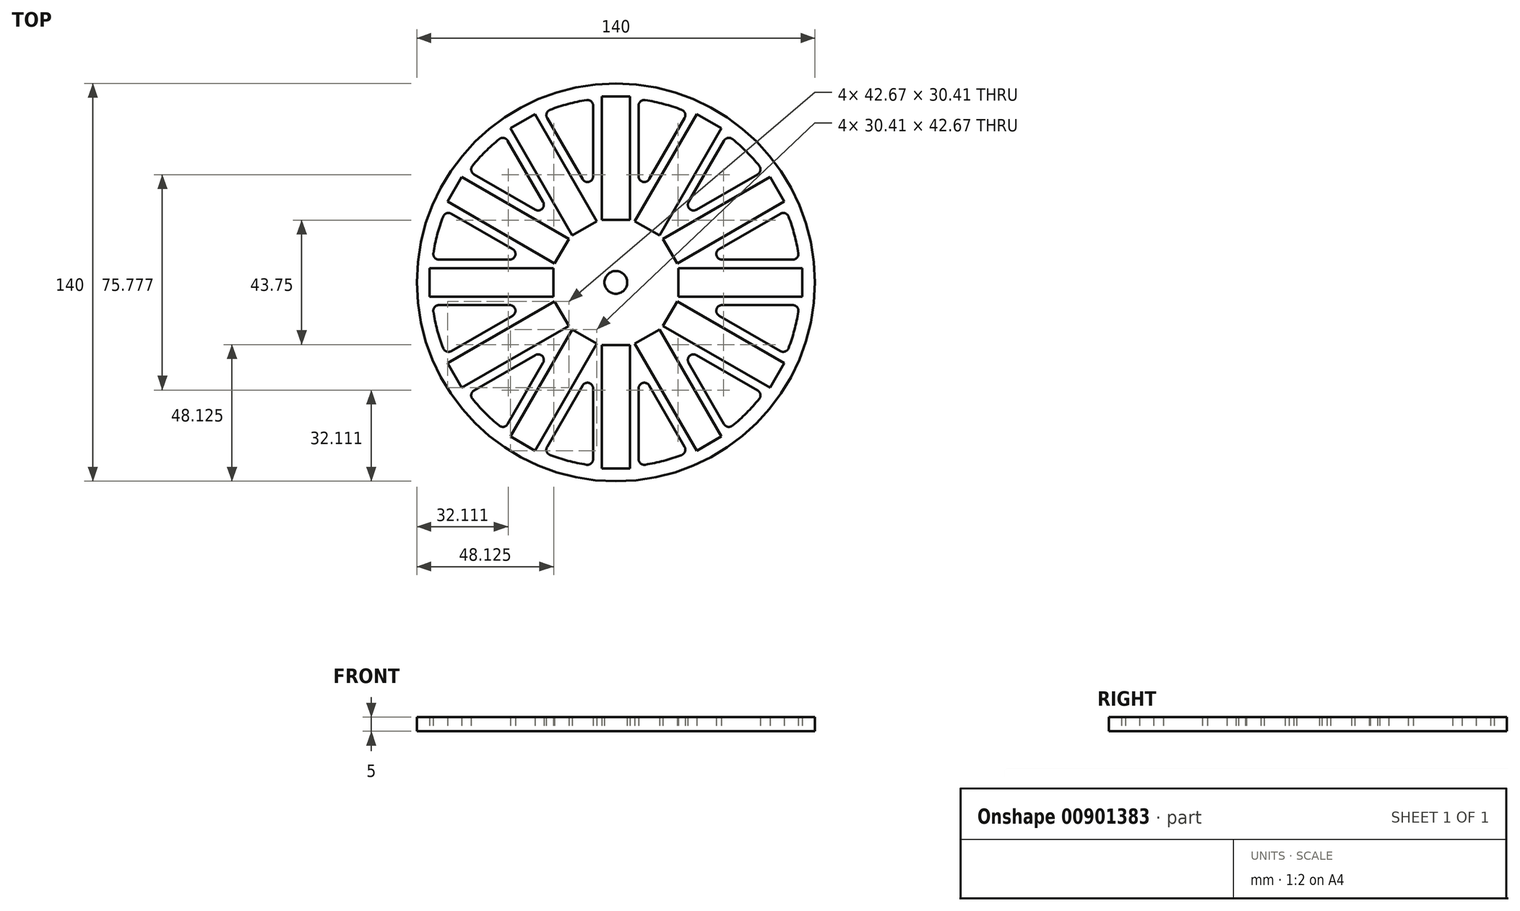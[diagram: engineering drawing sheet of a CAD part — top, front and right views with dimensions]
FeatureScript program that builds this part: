
annotation { "Feature Type Name" : "Feature", "Feature Type Description" : "" }
export const myFeature = defineFeature(function(context is Context, id is Id, definition is map)
    precondition{}
    {
        {
            var Q0;
            Q0=qCreatedBy(makeId("Top.planeOp"),FACE);
            var sketch = newSketch(context, id + "F0", { "sketchPlane" : qUnion([Q0])});
            skLineSegment(sketch, "E0.bottom", {"start": v(65.5, 5) * mm, "end": v(22, 5) * mm});
            skLineSegment(sketch, "E0.top", {"start": v(65.5, -5) * mm, "end": v(22, -5) * mm});
            skLineSegment(sketch, "E0.left", {"start": v(65.5, 5) * mm, "end": v(65.5, -5) * mm});
            skLineSegment(sketch, "E0.right", {"start": v(22, 5) * mm, "end": v(22, -5) * mm});
            skCircle(sketch, "E1", {"center": v(0, 0) * mm, "radius": 4 * mm});
            skLineSegment(sketch, "E2.1.0", {"start": v(54.22, 37.08) * mm, "end": v(59.22, 28.42) * mm});
            skLineSegment(sketch, "E2.1.1", {"start": v(54.22, 37.08) * mm, "end": v(16.55, 15.33) * mm});
            skLineSegment(sketch, "E2.1.2", {"start": v(59.22, 28.42) * mm, "end": v(21.55, 6.67) * mm});
            skLineSegment(sketch, "E2.1.3", {"start": v(16.55, 15.33) * mm, "end": v(21.55, 6.67) * mm});
            skLineSegment(sketch, "E2.2.0", {"start": v(28.42, 59.22) * mm, "end": v(37.08, 54.22) * mm});
            skLineSegment(sketch, "E2.2.1", {"start": v(28.42, 59.22) * mm, "end": v(6.67, 21.55) * mm});
            skLineSegment(sketch, "E2.2.2", {"start": v(37.08, 54.22) * mm, "end": v(15.33, 16.55) * mm});
            skLineSegment(sketch, "E2.2.3", {"start": v(6.67, 21.55) * mm, "end": v(15.33, 16.55) * mm});
            skLineSegment(sketch, "E2.3.0", {"start": v(-5, 65.5) * mm, "end": v(5, 65.5) * mm});
            skLineSegment(sketch, "E2.3.1", {"start": v(-5, 65.5) * mm, "end": v(-5, 22) * mm});
            skLineSegment(sketch, "E2.3.2", {"start": v(5, 65.5) * mm, "end": v(5, 22) * mm});
            skLineSegment(sketch, "E2.3.3", {"start": v(-5, 22) * mm, "end": v(5, 22) * mm});
            skLineSegment(sketch, "E2.4.0", {"start": v(-37.08, 54.22) * mm, "end": v(-28.42, 59.22) * mm});
            skLineSegment(sketch, "E2.4.1", {"start": v(-37.08, 54.22) * mm, "end": v(-15.33, 16.55) * mm});
            skLineSegment(sketch, "E2.4.2", {"start": v(-28.42, 59.22) * mm, "end": v(-6.67, 21.55) * mm});
            skLineSegment(sketch, "E2.4.3", {"start": v(-15.33, 16.55) * mm, "end": v(-6.67, 21.55) * mm});
            skLineSegment(sketch, "E2.5.0", {"start": v(-59.22, 28.42) * mm, "end": v(-54.22, 37.08) * mm});
            skLineSegment(sketch, "E2.5.1", {"start": v(-59.22, 28.42) * mm, "end": v(-21.55, 6.67) * mm});
            skLineSegment(sketch, "E2.5.2", {"start": v(-54.22, 37.08) * mm, "end": v(-16.55, 15.33) * mm});
            skLineSegment(sketch, "E2.5.3", {"start": v(-21.55, 6.67) * mm, "end": v(-16.55, 15.33) * mm});
            skLineSegment(sketch, "E2.6.0", {"start": v(-65.5, -5) * mm, "end": v(-65.5, 5) * mm});
            skLineSegment(sketch, "E2.6.1", {"start": v(-65.5, -5) * mm, "end": v(-22, -5) * mm});
            skLineSegment(sketch, "E2.6.2", {"start": v(-65.5, 5) * mm, "end": v(-22, 5) * mm});
            skLineSegment(sketch, "E2.6.3", {"start": v(-22, -5) * mm, "end": v(-22, 5) * mm});
            skLineSegment(sketch, "E2.7.0", {"start": v(-54.22, -37.08) * mm, "end": v(-59.22, -28.42) * mm});
            skLineSegment(sketch, "E2.7.1", {"start": v(-54.22, -37.08) * mm, "end": v(-16.55, -15.33) * mm});
            skLineSegment(sketch, "E2.7.2", {"start": v(-59.22, -28.42) * mm, "end": v(-21.55, -6.67) * mm});
            skLineSegment(sketch, "E2.7.3", {"start": v(-16.55, -15.33) * mm, "end": v(-21.55, -6.67) * mm});
            skLineSegment(sketch, "E2.8.0", {"start": v(-28.42, -59.22) * mm, "end": v(-37.08, -54.22) * mm});
            skLineSegment(sketch, "E2.8.1", {"start": v(-28.42, -59.22) * mm, "end": v(-6.67, -21.55) * mm});
            skLineSegment(sketch, "E2.8.2", {"start": v(-37.08, -54.22) * mm, "end": v(-15.33, -16.55) * mm});
            skLineSegment(sketch, "E2.8.3", {"start": v(-6.67, -21.55) * mm, "end": v(-15.33, -16.55) * mm});
            skLineSegment(sketch, "E2.9.0", {"start": v(5, -65.5) * mm, "end": v(-5, -65.5) * mm});
            skLineSegment(sketch, "E2.9.1", {"start": v(5, -65.5) * mm, "end": v(5, -22) * mm});
            skLineSegment(sketch, "E2.9.2", {"start": v(-5, -65.5) * mm, "end": v(-5, -22) * mm});
            skLineSegment(sketch, "E2.9.3", {"start": v(5, -22) * mm, "end": v(-5, -22) * mm});
            skLineSegment(sketch, "E2.10.0", {"start": v(37.08, -54.22) * mm, "end": v(28.42, -59.22) * mm});
            skLineSegment(sketch, "E2.10.1", {"start": v(37.08, -54.22) * mm, "end": v(15.33, -16.55) * mm});
            skLineSegment(sketch, "E2.10.2", {"start": v(28.42, -59.22) * mm, "end": v(6.67, -21.55) * mm});
            skLineSegment(sketch, "E2.10.3", {"start": v(15.33, -16.55) * mm, "end": v(6.67, -21.55) * mm});
            skLineSegment(sketch, "E2.11.0", {"start": v(59.22, -28.42) * mm, "end": v(54.22, -37.08) * mm});
            skLineSegment(sketch, "E2.11.1", {"start": v(59.22, -28.42) * mm, "end": v(21.55, -6.67) * mm});
            skLineSegment(sketch, "E2.11.2", {"start": v(54.22, -37.08) * mm, "end": v(16.55, -15.33) * mm});
            skLineSegment(sketch, "E2.11.3", {"start": v(21.55, -6.67) * mm, "end": v(16.55, -15.33) * mm});
            skLineSegment(sketch, "E3.0", {"start": v(-24.17, 57.87) * mm, "end": v(-11.73, 36.32) * mm});
            skLineSegment(sketch, "E4.0", {"start": v(-8, 62.2) * mm, "end": v(-8, 37.32) * mm});
            skLineSegment(sketch, "E5.0", {"start": v(8, 62.2) * mm, "end": v(8, 37.32) * mm});
            skLineSegment(sketch, "E6.0", {"start": v(24.17, 57.87) * mm, "end": v(11.73, 36.32) * mm});
            skLineSegment(sketch, "E7.0", {"start": v(62.2, 8) * mm, "end": v(37.32, 8) * mm});
            skLineSegment(sketch, "E8.0", {"start": v(57.87, -24.17) * mm, "end": v(36.32, -11.73) * mm});
            skLineSegment(sketch, "E9.0", {"start": v(38.03, -49.87) * mm, "end": v(25.59, -28.32) * mm});
            skLineSegment(sketch, "E10.0", {"start": v(8, -62.2) * mm, "end": v(8, -37.32) * mm});
            skLineSegment(sketch, "E11.0", {"start": v(-24.17, -57.87) * mm, "end": v(-11.73, -36.32) * mm});
            skLineSegment(sketch, "E12.0", {"start": v(-49.87, -38.03) * mm, "end": v(-28.32, -25.59) * mm});
            skLineSegment(sketch, "E13.0", {"start": v(-62.2, -8) * mm, "end": v(-37.32, -8) * mm});
            skLineSegment(sketch, "E14.0", {"start": v(-57.87, 24.17) * mm, "end": v(-36.32, 11.73) * mm});
            skLineSegment(sketch, "E15.0", {"start": v(-38.03, 49.87) * mm, "end": v(-25.59, 28.32) * mm});
            skLineSegment(sketch, "E16.0", {"start": v(-49.87, 38.03) * mm, "end": v(-28.32, 25.59) * mm});
            skLineSegment(sketch, "E17.0", {"start": v(-57.87, -24.17) * mm, "end": v(-36.32, -11.73) * mm});
            skLineSegment(sketch, "E18.0", {"start": v(-38.03, -49.87) * mm, "end": v(-25.59, -28.32) * mm});
            skLineSegment(sketch, "E19.0", {"start": v(-8, -62.2) * mm, "end": v(-8, -37.32) * mm});
            skLineSegment(sketch, "E20.0", {"start": v(24.17, -57.87) * mm, "end": v(11.73, -36.32) * mm});
            skLineSegment(sketch, "E21.0", {"start": v(49.87, -38.03) * mm, "end": v(28.32, -25.59) * mm});
            skLineSegment(sketch, "E22.0", {"start": v(62.2, -8) * mm, "end": v(37.32, -8) * mm});
            skLineSegment(sketch, "E23.0", {"start": v(57.87, 24.17) * mm, "end": v(36.32, 11.73) * mm});
            skLineSegment(sketch, "E24.0", {"start": v(38.03, 49.87) * mm, "end": v(25.59, 28.32) * mm});
            skLineSegment(sketch, "E25.0", {"start": v(-62.2, 8) * mm, "end": v(-37.32, 8) * mm});
            skLineSegment(sketch, "E26.0", {"start": v(49.87, 38.03) * mm, "end": v(28.32, 25.59) * mm});
            skPoint(sketch, "E27.visualSharp", {"position": v(-8, 29.86) * mm});
            skArc(sketch, "E27.filletArc", {"start": v(-11.73, 36.32) * mm, "mid": v(-9.48, 35.39) * mm, "end": v(-8, 37.32) * mm});
            skPoint(sketch, "E28.visualSharp", {"position": v(-21.86, 21.86) * mm});
            skArc(sketch, "E28.filletArc", {"start": v(-28.32, 25.59) * mm, "mid": v(-25.9, 25.9) * mm, "end": v(-25.59, 28.32) * mm});
            skPoint(sketch, "E29.visualSharp", {"position": v(-29.86, 8) * mm});
            skArc(sketch, "E29.filletArc", {"start": v(-37.32, 8) * mm, "mid": v(-35.39, 9.48) * mm, "end": v(-36.32, 11.73) * mm});
            skPoint(sketch, "E30.visualSharp", {"position": v(-21.86, -21.86) * mm});
            skArc(sketch, "E30.filletArc", {"start": v(-25.59, -28.32) * mm, "mid": v(-25.9, -25.9) * mm, "end": v(-28.32, -25.59) * mm});
            skPoint(sketch, "E31.visualSharp", {"position": v(-8, -29.86) * mm});
            skArc(sketch, "E31.filletArc", {"start": v(-8, -37.32) * mm, "mid": v(-9.48, -35.39) * mm, "end": v(-11.73, -36.32) * mm});
            skPoint(sketch, "E32.visualSharp", {"position": v(8, -29.86) * mm});
            skArc(sketch, "E32.filletArc", {"start": v(11.73, -36.32) * mm, "mid": v(9.48, -35.39) * mm, "end": v(8, -37.32) * mm});
            skPoint(sketch, "E33.visualSharp", {"position": v(21.86, -21.86) * mm});
            skArc(sketch, "E33.filletArc", {"start": v(28.32, -25.59) * mm, "mid": v(25.9, -25.9) * mm, "end": v(25.59, -28.32) * mm});
            skPoint(sketch, "E34.visualSharp", {"position": v(29.86, -8) * mm});
            skArc(sketch, "E34.filletArc", {"start": v(37.32, -8) * mm, "mid": v(35.39, -9.48) * mm, "end": v(36.32, -11.73) * mm});
            skPoint(sketch, "E35.visualSharp", {"position": v(29.86, 8) * mm});
            skArc(sketch, "E35.filletArc", {"start": v(36.32, 11.73) * mm, "mid": v(35.39, 9.48) * mm, "end": v(37.32, 8) * mm});
            skPoint(sketch, "E36.visualSharp", {"position": v(21.86, 21.86) * mm});
            skArc(sketch, "E36.filletArc", {"start": v(25.59, 28.32) * mm, "mid": v(25.9, 25.9) * mm, "end": v(28.32, 25.59) * mm});
            skPoint(sketch, "E37.visualSharp", {"position": v(8, 29.86) * mm});
            skArc(sketch, "E37.filletArc", {"start": v(8, 37.32) * mm, "mid": v(9.48, 35.39) * mm, "end": v(11.73, 36.32) * mm});
            skPoint(sketch, "E38.visualSharp", {"position": v(-29.86, -8) * mm});
            skArc(sketch, "E38.filletArc", {"start": v(-36.32, -11.73) * mm, "mid": v(-35.39, -9.48) * mm, "end": v(-37.32, -8) * mm});
            skCircle(sketch, "E39", {"center": v(0, 0) * mm, "radius": 70 * mm});
            skArc(sketch, "E40", {"start": v(50.42, 41.02) * mm, "mid": v(45.96, 45.96) * mm, "end": v(41.02, 50.42) * mm});
            skArc(sketch, "E41.trimOffspring", {"start": v(64.18, 10.32) * mm, "mid": v(62.79, 16.82) * mm, "end": v(60.74, 23.15) * mm});
            skArc(sketch, "E42.trimOffspring", {"start": v(60.74, -23.15) * mm, "mid": v(62.79, -16.82) * mm, "end": v(64.18, -10.32) * mm});
            skArc(sketch, "E43.trimOffspring", {"start": v(41.02, -50.42) * mm, "mid": v(45.96, -45.96) * mm, "end": v(50.42, -41.02) * mm});
            skArc(sketch, "E44.trimOffspring", {"start": v(10.32, -64.18) * mm, "mid": v(16.82, -62.79) * mm, "end": v(23.15, -60.74) * mm});
            skArc(sketch, "E45.trimOffspring", {"start": v(-23.15, -60.74) * mm, "mid": v(-16.82, -62.79) * mm, "end": v(-10.32, -64.18) * mm});
            skArc(sketch, "E46.trimOffspring", {"start": v(-50.42, -41.02) * mm, "mid": v(-45.96, -45.96) * mm, "end": v(-41.02, -50.42) * mm});
            skArc(sketch, "E47.trimOffspring", {"start": v(-64.18, -10.32) * mm, "mid": v(-62.79, -16.82) * mm, "end": v(-60.74, -23.15) * mm});
            skArc(sketch, "E48.trimOffspring", {"start": v(-60.74, 23.15) * mm, "mid": v(-62.79, 16.82) * mm, "end": v(-64.18, 10.32) * mm});
            skArc(sketch, "E49.trimOffspring", {"start": v(-41.02, 50.42) * mm, "mid": v(-45.96, 45.96) * mm, "end": v(-50.42, 41.02) * mm});
            skArc(sketch, "E50.trimOffspring", {"start": v(-10.32, 64.18) * mm, "mid": v(-16.82, 62.79) * mm, "end": v(-23.15, 60.74) * mm});
            skArc(sketch, "E51.trimOffspring", {"start": v(23.15, 60.74) * mm, "mid": v(16.82, 62.79) * mm, "end": v(10.32, 64.18) * mm});
            skPoint(sketch, "E52.visualSharp", {"position": v(-8, 64.5) * mm});
            skArc(sketch, "E52.filletArc", {"start": v(-8, 62.2) * mm, "mid": v(-8.7, 63.72) * mm, "end": v(-10.32, 64.18) * mm});
            skPoint(sketch, "E53.visualSharp", {"position": v(-25.32, 59.86) * mm});
            skArc(sketch, "E53.filletArc", {"start": v(-23.15, 60.74) * mm, "mid": v(-24.32, 59.54) * mm, "end": v(-24.17, 57.87) * mm});
            skPoint(sketch, "E54.visualSharp", {"position": v(-39.18, 51.86) * mm});
            skArc(sketch, "E54.filletArc", {"start": v(-38.03, 49.87) * mm, "mid": v(-39.4, 50.83) * mm, "end": v(-41.02, 50.42) * mm});
            skPoint(sketch, "E55.visualSharp", {"position": v(-51.86, 39.18) * mm});
            skArc(sketch, "E55.filletArc", {"start": v(-50.42, 41.02) * mm, "mid": v(-50.83, 39.4) * mm, "end": v(-49.87, 38.03) * mm});
            skPoint(sketch, "E56.visualSharp", {"position": v(-59.86, 25.32) * mm});
            skArc(sketch, "E56.filletArc", {"start": v(-57.87, 24.17) * mm, "mid": v(-59.54, 24.32) * mm, "end": v(-60.74, 23.15) * mm});
            skPoint(sketch, "E57.visualSharp", {"position": v(-64.5, 8) * mm});
            skArc(sketch, "E57.filletArc", {"start": v(-64.18, 10.32) * mm, "mid": v(-63.72, 8.7) * mm, "end": v(-62.2, 8) * mm});
            skPoint(sketch, "E58.visualSharp", {"position": v(-64.5, -8) * mm});
            skArc(sketch, "E58.filletArc", {"start": v(-62.2, -8) * mm, "mid": v(-63.72, -8.7) * mm, "end": v(-64.18, -10.32) * mm});
            skPoint(sketch, "E59.visualSharp", {"position": v(-59.86, -25.32) * mm});
            skArc(sketch, "E59.filletArc", {"start": v(-60.74, -23.15) * mm, "mid": v(-59.54, -24.32) * mm, "end": v(-57.87, -24.17) * mm});
            skPoint(sketch, "E60.visualSharp", {"position": v(-51.86, -39.18) * mm});
            skArc(sketch, "E60.filletArc", {"start": v(-49.87, -38.03) * mm, "mid": v(-50.83, -39.4) * mm, "end": v(-50.42, -41.02) * mm});
            skPoint(sketch, "E61.visualSharp", {"position": v(-39.18, -51.86) * mm});
            skArc(sketch, "E61.filletArc", {"start": v(-41.02, -50.42) * mm, "mid": v(-39.4, -50.83) * mm, "end": v(-38.03, -49.87) * mm});
            skPoint(sketch, "E62.visualSharp", {"position": v(-25.32, -59.86) * mm});
            skArc(sketch, "E62.filletArc", {"start": v(-24.17, -57.87) * mm, "mid": v(-24.32, -59.54) * mm, "end": v(-23.15, -60.74) * mm});
            skPoint(sketch, "E63.visualSharp", {"position": v(-8, -64.5) * mm});
            skArc(sketch, "E63.filletArc", {"start": v(-10.32, -64.18) * mm, "mid": v(-8.7, -63.72) * mm, "end": v(-8, -62.2) * mm});
            skPoint(sketch, "E64.visualSharp", {"position": v(8, -64.5) * mm});
            skArc(sketch, "E64.filletArc", {"start": v(8, -62.2) * mm, "mid": v(8.7, -63.72) * mm, "end": v(10.32, -64.18) * mm});
            skPoint(sketch, "E65.visualSharp", {"position": v(25.32, -59.86) * mm});
            skArc(sketch, "E65.filletArc", {"start": v(23.15, -60.74) * mm, "mid": v(24.32, -59.54) * mm, "end": v(24.17, -57.87) * mm});
            skPoint(sketch, "E66.visualSharp", {"position": v(39.18, -51.86) * mm});
            skArc(sketch, "E66.filletArc", {"start": v(38.03, -49.87) * mm, "mid": v(39.4, -50.83) * mm, "end": v(41.02, -50.42) * mm});
            skPoint(sketch, "E67.visualSharp", {"position": v(51.86, -39.18) * mm});
            skArc(sketch, "E67.filletArc", {"start": v(50.42, -41.02) * mm, "mid": v(50.83, -39.4) * mm, "end": v(49.87, -38.03) * mm});
            skPoint(sketch, "E68.visualSharp", {"position": v(64.5, -8) * mm});
            skArc(sketch, "E68.filletArc", {"start": v(64.18, -10.32) * mm, "mid": v(63.72, -8.7) * mm, "end": v(62.2, -8) * mm});
            skPoint(sketch, "E69.visualSharp", {"position": v(59.86, -25.32) * mm});
            skArc(sketch, "E69.filletArc", {"start": v(57.87, -24.17) * mm, "mid": v(59.54, -24.32) * mm, "end": v(60.74, -23.15) * mm});
            skPoint(sketch, "E70.visualSharp", {"position": v(59.86, 25.32) * mm});
            skArc(sketch, "E70.filletArc", {"start": v(60.74, 23.15) * mm, "mid": v(59.54, 24.32) * mm, "end": v(57.87, 24.17) * mm});
            skPoint(sketch, "E71.visualSharp", {"position": v(64.5, 8) * mm});
            skArc(sketch, "E71.filletArc", {"start": v(62.2, 8) * mm, "mid": v(63.72, 8.7) * mm, "end": v(64.18, 10.32) * mm});
            skPoint(sketch, "E72.visualSharp", {"position": v(39.18, 51.86) * mm});
            skArc(sketch, "E72.filletArc", {"start": v(41.02, 50.42) * mm, "mid": v(39.4, 50.83) * mm, "end": v(38.03, 49.87) * mm});
            skPoint(sketch, "E73.visualSharp", {"position": v(51.86, 39.18) * mm});
            skArc(sketch, "E73.filletArc", {"start": v(49.87, 38.03) * mm, "mid": v(50.83, 39.4) * mm, "end": v(50.42, 41.02) * mm});
            skPoint(sketch, "E74.visualSharp", {"position": v(25.32, 59.86) * mm});
            skArc(sketch, "E74.filletArc", {"start": v(24.17, 57.87) * mm, "mid": v(24.32, 59.54) * mm, "end": v(23.15, 60.74) * mm});
            skPoint(sketch, "E75.visualSharp", {"position": v(8, 64.5) * mm});
            skArc(sketch, "E75.filletArc", {"start": v(10.32, 64.18) * mm, "mid": v(8.7, 63.72) * mm, "end": v(8, 62.2) * mm});
            skSolve(sketch);
        }
        {
            var Q0;
            Q0=makeQuery(id+"F0.imprint","IMPRINT",FACE,{"disambiguationData":[TD([[makeQuery(id+"F0.imprint","IMPRINT",EDGE,{"derivedFrom":sQuery(id+"F0.wireOp",EDGE,"E0.bottom")}),-1.0]])]});
            extrude(context, id + "F1", {"entities" : qUnion([Q0]), "depth" : 5 * mm, "offsetDistance" : 25 * mm});
        }
    });
